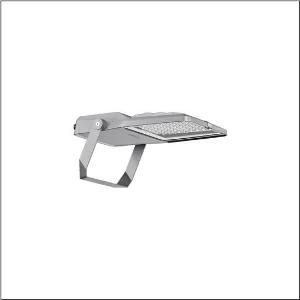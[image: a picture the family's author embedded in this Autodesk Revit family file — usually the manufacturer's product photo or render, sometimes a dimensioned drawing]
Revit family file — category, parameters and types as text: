
# Revit family: floodlight_fl_21_iq_mini___pl61_5xa7772d2c1a_0e67
name_source: partatom
category: Lighting Fixtures
units: mm (PartAtom-declared; Revit-internal decimal feet)

## family parameters
Cut with Voids When Loaded = No
Host = Face
Light Source = No
Part Type = Normal
Room Calculation Point = No
Round Connector Dimension = Use Diameter
Shared = No

## types (1)
- --- (1 x LED, 17500 lm, 143 W, 3000K)
    Apparent Load = 143 VA
    CIE Flux Codes = 33 65 98 100 100
    Color Rendering = 70
    Color Temperature = 3000K
    Default Elevation = 1800 mm
    Description = Floodlight FL 21 iQ mini, floodlight, primary light control with lens, of PMMA, primary optical cover: protective disc, of toughened safety glass, transparent, light distribution: PL61, light emission: direct distribution, installation type: surface-mounted, lamps: LED, High Power LED, rated values: 17.500lm | 143W | 122,4lm/W (begin service life); end service life: 17.500lm | 151,6W; at 50% lumin. flux: 8.750lm | 60,6W | 144,4lm/W, colour temperature: 3000K, colour rendering: CRI > 70, light colour: 730, light setting 1 begin service life: 100% | 17.500lm | 143W | 122,4lm/W | 3.000K, light setting 1 end service life: 151,6W, further light settings possible, control: Street-Remote, Auto-Match, Temp-Guard, Night-Set, Smart-Wire, Desk-Remote (wireless, voltage-free reading and setting of iQ features in the workshop via application-optimized NFC function/RFID function), optimised constant luminous flux control (CLO 2.0), pre-setting: linear dimming characteristic, with terminal, 6-pole, mains connection: 220..240V, AC, 50/60Hz, luminaire housing, of diecast aluminium, powder-coated, SITECO metallic grey (DB 702S), corrosivity category C5 mid according to DIN EN ISO 12944suitable for swimming poolschlorine-resistant, sealing non-destructively replaceable, mounting bracket, of steel, galvanised, powder-coated, SITECO metallic grey (DB 702S), protection rating (complete): IP66, insulation class (complete): insulation class II (safety insulation), certification: CE, ENEC, VDE, protection symbol: D, impact resistance: IK08, permissible operating ambient temperature: -40..+40°C, permissible operating ambient temperature for outdoor applications: -40..+50°C, standard: DIN EN 12944, LABS conformity tested according to VDMA 24364:2018-05, packaging unit: 1 piece

Light Distribution: PL61
    Height = 70 mm
    Lamp = 1 x LED
    Lamp Light Flux = 17500 lm
    Lamp Power = 143 W
    Lamp count = 1
    Length = 485 mm
    Luminous efficacy = 122 lm/W
    Manufacturer = Siteco
    ModVariant = No
    Model = 5XA7772D2C1A
    Mounting Place = Pole
    Mounting Type = Pole annexe
    Number of Poles = 1
    OnlyDefault = Yes
    Power Factor = 1
    Product Name = Floodlight FL 21 iQ mini | PL61
    Product group = floodlight | pylon annexe
    ProductGroupID = 6201
    Protection Class = Protection class II
    Protection Degree = IP 66
    RLX_Detail_Level = 1
    RLX_Emergency_Light_Flux = 0 lm
    RLX_Emergency_Type = 0
    RLX_Emergency_Type_DB = No
    RlxData = <blob elided: 96857 chars, md5=6d2251b7>
    Socket = socket
    Standby Power = 0 W
    System Light Flux = 17500 lm
    System Power = 143 W
    Type Comments = factory setting: luminous flux: 100 % | dim-lin: 254 | 730 mA
    Type Image = l_1006845.jpg
    URL = http://relux.com
    VarID = @adj_173569
    Voltage = 0 V
    Weight = 0.00 kg
    Width = 337 mm

## geometry (parser evidence)
native form markers: Blend x4, Sweep x11
no freeform markers — native parametric forms only
